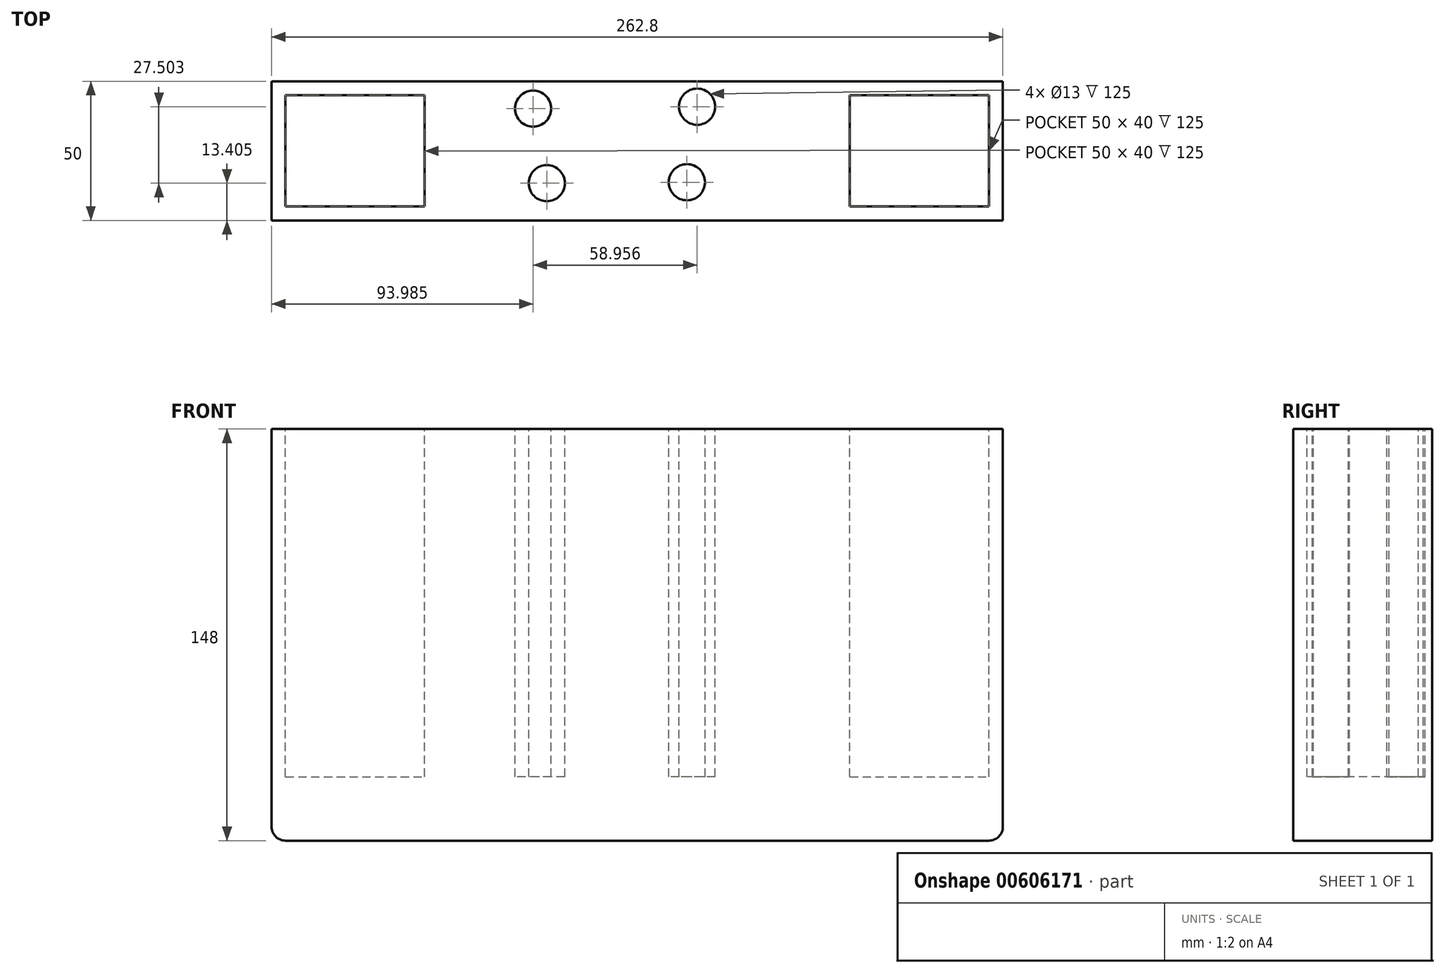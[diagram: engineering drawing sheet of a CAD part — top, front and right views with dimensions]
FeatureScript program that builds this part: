
annotation { "Feature Type Name" : "Feature", "Feature Type Description" : "" }
export const myFeature = defineFeature(function(context is Context, id is Id, definition is map)
    precondition{}
    {
        {
            var Q0;
            Q0=qCreatedBy(makeId("Front.planeOp"),FACE);
            var sketch = newSketch(context, id + "F0", { "sketchPlane" : qUnion([Q0])});
            skLineSegment(sketch, "E0.top", {"start": v(-56.4, -18) * mm, "end": v(206.4, -18) * mm});
            skLineSegment(sketch, "E1.top", {"start": v(-58.4, 130) * mm, "end": v(-56.4, 130) * mm});
            skLineSegment(sketch, "E1.right", {"start": v(-56.4, -18) * mm, "end": v(-56.4, 130) * mm});
            skLineSegment(sketch, "E2.top", {"start": v(208.4, 130) * mm, "end": v(206.4, 130) * mm});
            skLineSegment(sketch, "E2.right", {"start": v(206.4, -18) * mm, "end": v(206.4, 130) * mm});
            skPoint(sketch, "E0.left.start.orphan", {"position": v(-58.4, -20) * mm});
            skLineSegment(sketch, "E3", {"start": v(-58.4, 130) * mm, "end": v(-58.4, -20) * mm});
            skPoint(sketch, "E2.bottom.start.orphan", {"position": v(211.6, -20) * mm});
            skLineSegment(sketch, "E4", {"start": v(208.4, 130) * mm, "end": v(211.6, -20) * mm});
            skLineSegment(sketch, "E5", {"start": v(-58.4, -20) * mm, "end": v(211.6, -20) * mm});
            skLineSegment(sketch, "E6", {"start": v(-56.4, 130) * mm, "end": v(206.4, 130) * mm});
            skSolve(sketch);
        }
        {
            var Q0;
            Q0=makeQuery(id+"F0.imprint","IMPRINT",FACE,{"disambiguationData":[TD([[makeQuery(id+"F0.imprint","IMPRINT",EDGE,{"derivedFrom":sQuery(id+"F0.wireOp",EDGE,"E0.top")}),1.0]])]});
            extrude(context, id + "F1", {"entities" : qUnion([Q0]), "depth" : 50 * mm, "offsetDistance" : 25 * mm});
        }
        {
            var Q0;
            Q0=makeQuery(id+"F1.opExtrude","SWEPT_EDGE",EDGE,{"disambiguationData":[OSD([sQuery(id+"F0.wireOp",EDGE,"E0.top"),sQuery(id+"F0.wireOp",EDGE,"E2.right")])]});
            fillet(context, id + "F2", {"entities" : qUnion([Q0]), "radius" : 5 * mm, "tangentPropagation" : true, "allowEdgeOverflow" : false});
        }
        {
            var Q0;
            Q0=makeQuery(id+"F1.opExtrude","SWEPT_EDGE",EDGE,{"disambiguationData":[OSD([sQuery(id+"F0.wireOp",EDGE,"E0.top"),sQuery(id+"F0.wireOp",EDGE,"E1.right")])]});
            fillet(context, id + "F3", {"entities" : qUnion([Q0]), "radius" : 5 * mm, "tangentPropagation" : true, "allowEdgeOverflow" : false});
        }
        {
            var Q0;
            Q0=makeQuery(id+"F1.opExtrude","SWEPT_FACE",FACE,{"disambiguationData":[OSD([sQuery(id+"F0.wireOp",EDGE,"E6")])]});
            var sketch = newSketch(context, id + "F4", { "sketchPlane" : qUnion([Q0])});
            skLineSegment(sketch, "E7.bottom", {"start": v(-51.4, -5) * mm, "end": v(-1.4, -5) * mm});
            skLineSegment(sketch, "E7.top", {"start": v(-51.4, -45) * mm, "end": v(-1.4, -45) * mm});
            skLineSegment(sketch, "E7.left", {"start": v(-51.4, -5) * mm, "end": v(-51.4, -45) * mm});
            skLineSegment(sketch, "E7.right", {"start": v(-1.4, -5) * mm, "end": v(-1.4, -45) * mm});
            skCircle(sketch, "E8", {"center": v(37.58, -9.79) * mm, "radius": 6.5 * mm});
            skCircle(sketch, "E9", {"center": v(96.54, -9.1) * mm, "radius": 6.5 * mm});
            skCircle(sketch, "E10", {"center": v(42.52, -36.6) * mm, "radius": 6.5 * mm});
            skCircle(sketch, "E11", {"center": v(92.87, -36.27) * mm, "radius": 6.5 * mm});
            skLineSegment(sketch, "E12.bottom", {"start": v(151.4, -5) * mm, "end": v(201.4, -5) * mm});
            skLineSegment(sketch, "E12.top", {"start": v(151.4, -45) * mm, "end": v(201.4, -45) * mm});
            skLineSegment(sketch, "E12.left", {"start": v(151.4, -5) * mm, "end": v(151.4, -45) * mm});
            skLineSegment(sketch, "E12.right", {"start": v(201.4, -5) * mm, "end": v(201.4, -45) * mm});
            skSolve(sketch);
        }
        {
            var Q0;
            Q0 = qSketchRegion(id + "F4", true);
            extrude(context, id + "F5", {"entities" : qUnion([Q0]), "operationType" : NewBodyOperationType.REMOVE, "oppositeDirection" : true, "depth" : 125 * mm, "offsetDistance" : 25 * mm});
        }
    });
